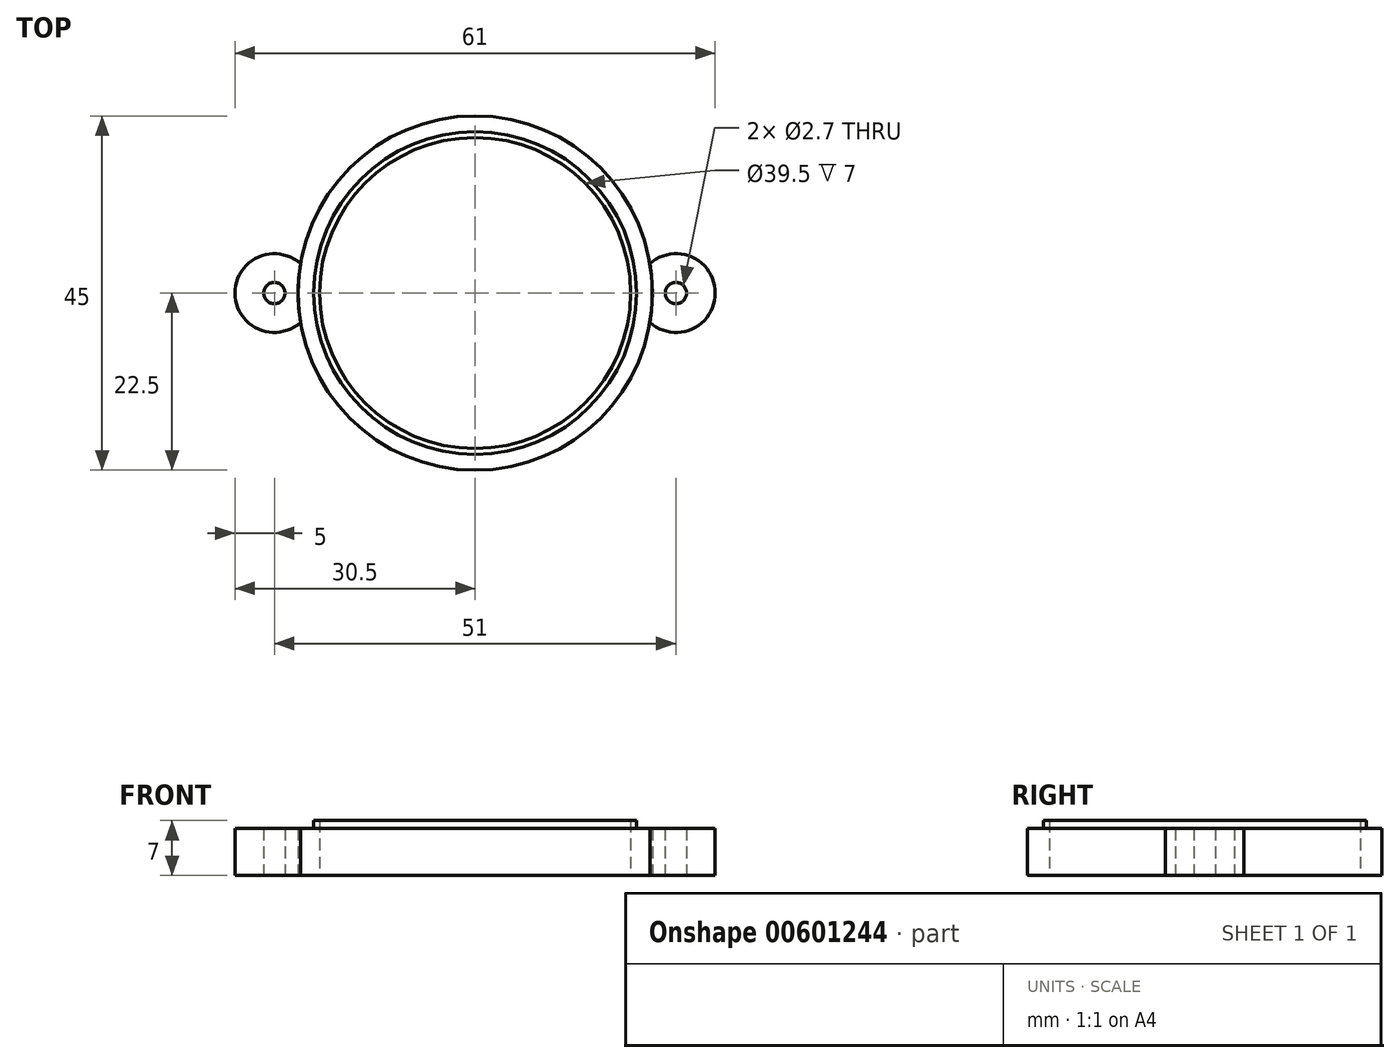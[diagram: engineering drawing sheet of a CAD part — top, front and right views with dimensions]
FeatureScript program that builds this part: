
annotation { "Feature Type Name" : "Feature", "Feature Type Description" : "" }
export const myFeature = defineFeature(function(context is Context, id is Id, definition is map)
    precondition{}
    {
        {
            var Q0;
            Q0=qCreatedBy(makeId("Top.planeOp"),FACE);
            var sketch = newSketch(context, id + "F0", { "sketchPlane" : qUnion([Q0])});
            skCircle(sketch, "E0", {"center": v(0, 0) * mm, "radius": 19.75 * mm});
            skCircle(sketch, "E1", {"center": v(0, 0) * mm, "radius": 22.5 * mm});
            skCircle(sketch, "E2", {"center": v(-25.5, 0) * mm, "radius": 5 * mm});
            skCircle(sketch, "E3", {"center": v(25.5, 0) * mm, "radius": 5 * mm});
            skCircle(sketch, "E4", {"center": v(-25.5, 0) * mm, "radius": 1.35 * mm});
            skCircle(sketch, "E5", {"center": v(25.5, 0) * mm, "radius": 1.35 * mm});
            skSolve(sketch);
        }
        {
            var Q0;
            Q0=makeQuery(id+"F0.imprint","IMPRINT",FACE,{"disambiguationData":[TD([[makeQuery(id+"F0.imprint","IMPRINT",EDGE,{"derivedFrom":sQuery(id+"F0.wireOp",EDGE,"E4")}),-1.0]])]});
            var Q1;
            Q1=makeQuery(id+"F0.imprint","IMPRINT",FACE,{"disambiguationData":[TD([[makeQuery(id+"F0.imprint","IMPRINT",EDGE,{"derivedFrom":sQuery(id+"F0.wireOp",EDGE,"E5")}),-1.0]])]});
            extrude(context, id + "F1", {"entities" : qUnion([Q0, Q1]), "depth" : 6 * mm, "offsetDistance" : 25 * mm});
        }
        {
            var Q0;
            Q0=makeQuery(id+"F0.imprint","IMPRINT",FACE,{"disambiguationData":[TD([[makeQuery(id+"F0.imprint","IMPRINT",EDGE,{"derivedFrom":sQuery(id+"F0.wireOp",EDGE,"E0")}),-1.0]])]});
            var Q1;
            {var subQ0=sQuery(id+"F0.wireOp",EDGE,"E2");var subQ1=sQuery(id+"F0.wireOp",EDGE,"E1");var subQ2=makeQuery(id+"F0.imprint","INTERSECT",VERTEX,{"disambiguationData":[OD(0.0)],"derivedFrom":[subQ1,subQ0]});Q1=makeQuery(id+"F0.imprint","IMPRINT",FACE,{"disambiguationData":[TD([[makeQuery(id+"F0.imprint","IMPRINT",EDGE,{"disambiguationData":[TD([[subQ2,-1.0]])],"derivedFrom":subQ1}),1.0]])]});}
            var Q2;
            {var subQ0=sQuery(id+"F0.wireOp",EDGE,"E3");var subQ1=sQuery(id+"F0.wireOp",EDGE,"E1");var subQ2=makeQuery(id+"F0.imprint","INTERSECT",VERTEX,{"disambiguationData":[OD(0.0)],"derivedFrom":[subQ1,subQ0]});Q2=makeQuery(id+"F0.imprint","IMPRINT",FACE,{"disambiguationData":[TD([[makeQuery(id+"F0.imprint","IMPRINT",EDGE,{"disambiguationData":[TD([[subQ2,1.0]])],"derivedFrom":subQ1}),1.0]])]});}
            extrude(context, id + "F2", {"entities" : qUnion([Q0, Q1, Q2]), "depth" : 6 * mm, "offsetDistance" : 25 * mm});
        }
        {
            var Q0;
            Q0=makeQuery(id+"F0.imprint","IMPRINT",FACE,{"disambiguationData":[TD([[makeQuery(id+"F0.imprint","IMPRINT",EDGE,{"derivedFrom":sQuery(id+"F0.wireOp",EDGE,"E0")}),1.0]])]});
            extrude(context, id + "F3", {"entities" : qUnion([Q0]), "depth" : 2 * mm, "offsetDistance" : 25 * mm});
        }
        {
            var Q0;
            Q0=makeQuery(id+"F3.opExtrude","SWEPT_BODY",BODY,{"disambiguationData":[OSD([sQuery(id+"F0.wireOp",EDGE,"E0")])]});
            deleteBodies(context, id + "F4", {"entities" : qUnion([Q0])});
        }
        {
            var Q0;
            Q0=makeQuery(id+"F2.opExtrude","CAP_FACE",FACE,{"disambiguationData":[OSD([sQuery(id+"F0.wireOp",EDGE,"E0"),sQuery(id+"F0.wireOp",EDGE,"E1")])],"isStart":false});
            var sketch = newSketch(context, id + "F5", { "sketchPlane" : qUnion([Q0])});
            skCircle(sketch, "E6", {"center": v(0, 0) * mm, "radius": 19.75 * mm});
            skCircle(sketch, "E7", {"center": v(0, 0) * mm, "radius": 20.5 * mm});
            skSolve(sketch);
        }
        {
            var Q0;
            Q0=makeQuery(id+"F5.imprint","IMPRINT",FACE,{"disambiguationData":[TD([[makeQuery(id+"F5.imprint","IMPRINT",EDGE,{"derivedFrom":sQuery(id+"F5.wireOp",EDGE,"E6")}),-1.0]])]});
            extrude(context, id + "F6", {"entities" : qUnion([Q0]), "operationType" : NewBodyOperationType.ADD, "depth" : 1 * mm, "offsetDistance" : 25 * mm});
        }
    });
